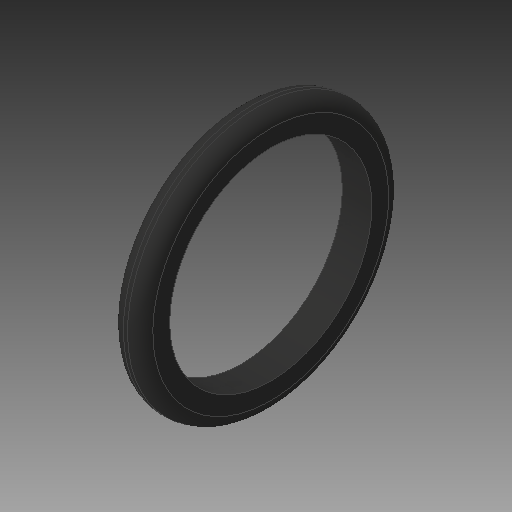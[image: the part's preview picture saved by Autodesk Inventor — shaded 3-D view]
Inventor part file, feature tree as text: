
AUTODESK INVENTOR PART (.ipt)
format: ipt  version: 2019.2 (Build 232265000, 265)  size: 155,136 bytes
history: native  units: mm
features: revolve x1, fillet x1, sketch x1
ambient origin geometry x8: Origin, YZ Plane, XZ Plane, XY Plane, X Axis, Y Axis, Z Axis, Center Point
bodies: Solid3 (feature_tree)
feature tree (3):
  revolve  "Revolution3"  [1 undecoded]
  fillet  "Fillet1"  Radius=70.0mm
  sketch  "Sketch5"  dims[d13=30.0mm d15=310.0mm d16=70.0mm d17=70.0mm d18=90.0deg]
note: 1 required parameter value undecoded (feature->parameter linkage not recoverable at this tier; creation-order binding heuristic only, values carry confidence <= 0.55)
